# Revit family: 305_D6_N
name_source: partatom
category: Pipe Accessories
units: mm (PartAtom-declared; Revit-internal decimal feet)

## family parameters
Always vertical = Yes
Cut with Voids When Loaded = No
Part Type = Valve - Breaks Into
Round Connector Dimension = Use Diameter
Shared = No
Work Plane-Based = No

## types (9) — shared parameters
CAT0 = Yes
Description = Butterfly valve, Wafer types, PN 6 / 10 / 16
L2D_Min = 3048 mm
Manufacturer = Belimo
QmdConnectorList = 301;D;302;D
magiPartTypeId = 305
magiProductFamilyId = D6*N
zero-valued in all types: MC_Default_elevation

## per-type parameters (varying)
| type | D | D1 | DBB | DD1 | H1 | H11 | H1__ve | H2 | H3 | H3__ve | L | L2D | LL | W2D |
| D6025N | 25 mm | 65 mm  [stored 0.213255 ft] | 60 mm  [stored 0.19685 ft] | 22 mm | 48 mm  [stored 0.15748 ft] | 76 mm | -48 mm  [stored -0.15748 ft] | 86 mm | 10 mm  [stored 0.0328084 ft] | -10 mm  [stored -0.0328084 ft] | 32 mm  [stored 0.104987 ft] | 32 mm  [stored 0.104987 ft] | 16 mm  [stored 0.0524934 ft] | 25 mm  [stored 0.082021 ft] |
| D6150N | 150 mm | 90 mm | 185 mm | 66 mm | 140 mm | 187 mm | -140 mm  [stored -0.459318 ft] | 202 mm | 15 mm  [stored 0.0492126 ft] | -15 mm  [stored -0.0492126 ft] | 56 mm  [stored 0.183727 ft] | 56 mm  [stored 0.183727 ft] | 28 mm  [stored 0.0918635 ft] | 150 mm |
| D6125N | 125 mm | 90 mm | 152 mm | 54 mm | 122 mm | 179 mm | -122 mm  [stored -0.400262 ft] | 194 mm | 15 mm  [stored 0.0492126 ft] | -15 mm  [stored -0.0492126 ft] | 56 mm  [stored 0.183727 ft] | 56 mm  [stored 0.183727 ft] | 28 mm  [stored 0.0918635 ft] | 125 mm |
| D6100N | 100 mm | 65 mm  [stored 0.213255 ft] | 133 mm | 48 mm  [stored 0.15748 ft] | 106 mm | 159 mm | -106 mm  [stored -0.347769 ft] | 170 mm | 11 mm  [stored 0.0360892 ft] | -11 mm  [stored -0.0360892 ft] | 52 mm  [stored 0.170604 ft] | 52 mm  [stored 0.170604 ft] | 26 mm  [stored 0.0853018 ft] | 100 mm |
| D6080N | 80 mm | 65 mm  [stored 0.213255 ft] | 108 mm | 39 mm | 96 mm | 147 mm | -96 mm  [stored -0.314961 ft] | 158 mm | 11 mm  [stored 0.0360892 ft] | -11 mm  [stored -0.0360892 ft] | 46 mm  [stored 0.150919 ft] | 46 mm  [stored 0.150919 ft] | 23 mm  [stored 0.0754593 ft] | 80 mm |
| D6065N | 65 mm | 65 mm  [stored 0.213255 ft] | 94 mm | 34 mm | 81 mm | 136 mm | -81 mm  [stored -0.265748 ft] | 147 mm | 11 mm  [stored 0.0360892 ft] | -11 mm  [stored -0.0360892 ft] | 46 mm  [stored 0.150919 ft] | 46 mm  [stored 0.150919 ft] | 23 mm  [stored 0.0754593 ft] | 65 mm  [stored 0.213255 ft] |
| D6050N | 50 mm | 65 mm  [stored 0.213255 ft] | 82 mm | 29 mm | 72 mm | 122 mm | -72 mm  [stored -0.23622 ft] | 133 mm | 11 mm  [stored 0.0360892 ft] | -11 mm  [stored -0.0360892 ft] | 43 mm  [stored 0.141076 ft] | 43 mm  [stored 0.141076 ft] | 22 mm | 50 mm  [stored 0.164042 ft] |
| D6040N | 40 mm | 65 mm  [stored 0.213255 ft] | 72 mm | 26 mm  [stored 0.0853018 ft] | 68 mm  [stored 0.223097 ft] | 109 mm | -68 mm  [stored -0.223097 ft] | 119 mm | 10 mm  [stored 0.0328084 ft] | -10 mm  [stored -0.0328084 ft] | 33 mm  [stored 0.108268 ft] | 33 mm  [stored 0.108268 ft] | 17 mm | 40 mm  [stored 0.131234 ft] |
| D6032N | 32 mm | 65 mm  [stored 0.213255 ft] | 65 mm  [stored 0.213255 ft] | 23 mm  [stored 0.0754593 ft] | 60 mm  [stored 0.19685 ft] | 90 mm | -60 mm  [stored -0.19685 ft] | 100 mm | 10 mm  [stored 0.0328084 ft] | -10 mm  [stored -0.0328084 ft] | 33 mm  [stored 0.108268 ft] | 33 mm  [stored 0.108268 ft] | 17 mm | 32 mm  [stored 0.104987 ft] |

note: column(s) folded — value = type name in every type: magiProductCode, magiProductId

note: [stored X ft] marks values corroborated as IEEE doubles in the binary element streams (Revit-internal decimal feet)

## geometry (parser evidence)
native form markers: Sweep x1
no freeform markers — native parametric forms only
